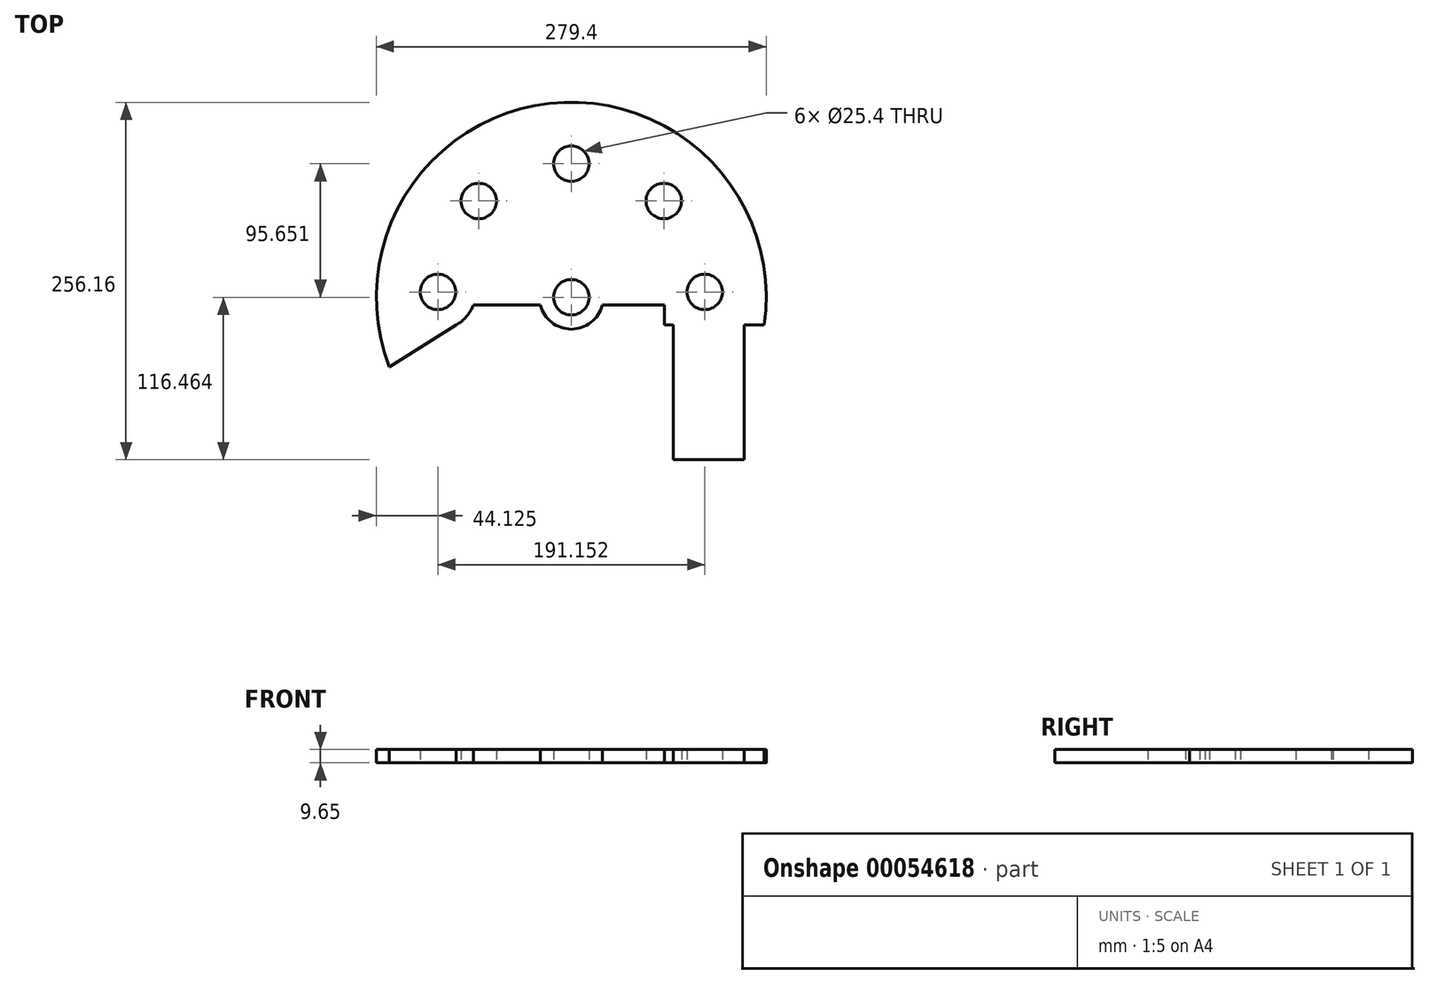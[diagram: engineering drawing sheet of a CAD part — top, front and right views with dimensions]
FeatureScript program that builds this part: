
annotation { "Feature Type Name" : "Feature", "Feature Type Description" : "" }
export const myFeature = defineFeature(function(context is Context, id is Id, definition is map)
    precondition{}
    {
        {
            var Q0;
            Q0=qCreatedBy(makeId("Top.planeOp"),FACE);
            var sketch = newSketch(context, id + "F0", { "sketchPlane" : qUnion([Q0])});
            skLineSegment(sketch, "E0", {"start": v(-65.19, 0) * mm, "end": v(-65.19, -96.52) * mm});
            skLineSegment(sketch, "E1", {"start": v(-65.19, -96.52) * mm, "end": v(-14.39, -96.52) * mm});
            skLineSegment(sketch, "E2", {"start": v(-14.39, -96.52) * mm, "end": v(-14.39, 0) * mm});
            skLineSegment(sketch, "E3", {"start": v(0, 0) * mm, "end": v(-14.39, 0) * mm});
            skLineSegment(sketch, "E4", {"start": v(-65.19, 0) * mm, "end": v(-71.65, 0) * mm});
            skLineSegment(sketch, "E5", {"start": v(-71.65, 0) * mm, "end": v(-71.65, 14.37) * mm});
            skLineSegment(sketch, "E6", {"start": v(-71.65, 14.37) * mm, "end": v(-116.1, 14.37) * mm});
            skArc(sketch, "E7", {"start": v(-160.44, 14.37) * mm, "mid": v(-138.27, -2.92) * mm, "end": v(-116.1, 14.37) * mm});
            skLineSegment(sketch, "E8", {"start": v(-160.44, 14.37) * mm, "end": v(-208.44, 14.37) * mm});
            skArc(sketch, "E9", {"start": v(-220.82, 0) * mm, "mid": v(-213.33, 6.07) * mm, "end": v(-208.44, 14.37) * mm});
            skLineSegment(sketch, "E10", {"start": v(-220.82, 0) * mm, "end": v(-220.82, 0) * mm});
            skLineSegment(sketch, "E11", {"start": v(-220.82, 0) * mm, "end": v(-268.72, -30.03) * mm});
            skArc(sketch, "E12", {"start": v(0, 0) * mm, "mid": v(-153.78, 158.78) * mm, "end": v(-268.72, -30.03) * mm});
            skCircle(sketch, "E13", {"center": v(-138.27, 19.94) * mm, "radius": 12.7 * mm});
            skCircle(sketch, "E14", {"center": v(-233.84, 23.73) * mm, "radius": 12.7 * mm});
            skCircle(sketch, "E15.1.0", {"center": v(-204.55, 88.9) * mm, "radius": 12.7 * mm});
            skCircle(sketch, "E15.2.0", {"center": v(-138.27, 115.6) * mm, "radius": 12.7 * mm});
            skCircle(sketch, "E15.3.0", {"center": v(-71.98, 88.9) * mm, "radius": 12.7 * mm});
            skCircle(sketch, "E15.4.0", {"center": v(-42.7, 23.73) * mm, "radius": 12.7 * mm});
            skLineSegment(sketch, "E15.anchor1", {"start": v(-138.27, 19.94) * mm, "end": v(-233.84, 23.73) * mm, "construction": true});
            skLineSegment(sketch, "E15.anchor2", {"start": v(-138.27, 19.94) * mm, "end": v(-42.7, 23.73) * mm, "construction": true});
            skSolve(sketch);
        }
        {
            var Q0;
            Q0 = qSketchRegion(id + "F0", true);
            extrude(context, id + "F1", {"entities" : qUnion([Q0]), "depth" : 9.65 * mm});
        }
    });
